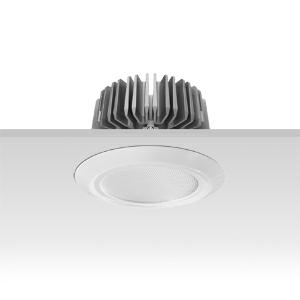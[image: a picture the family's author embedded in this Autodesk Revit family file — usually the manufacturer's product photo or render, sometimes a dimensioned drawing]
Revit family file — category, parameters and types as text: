
# Revit family: 3f_filippi_-_3f_reno_bianco_ampio_3f_filippi_-_30379_a01046_-_3f_reno_150_wh_2000-930_dali_wide___smp_wh_20f6
name_source: partatom
category: Lighting Fixtures
units: mm (PartAtom-declared; Revit-internal decimal feet)

## family parameters
Cut with Voids When Loaded = No
Host = Face
Light Source = No
Part Type = Normal
Room Calculation Point = No
Round Connector Dimension = Use Diameter
Shared = No

## types (1)
- 3F Filippi - 3F Reno Bianco Ampio (1 x LED, 1652 lm, 24 W, 3000 K)
    Apparent Load = 24 VA
    Approval mark = CE
    CIE Flux Codes = 73 92 98 100 100
    Color Rendering = 90
    Color Temperature = 3000 K
    Control Gear = Electronic transformer
    Default Elevation = 1800 mm
    Description = ILLUMINOTECHNICAL
Luminous efficiency 100% (DLOR 100%, ULOR 0%).
Initial luminous flux of the luminaire 1652 lm.
Direct symmetric wide distribution.
Installation Interdistance Transv.D = 1.01 x hu - Long.D = 1.00 x hu.
Tabular UGR (CIE 117 - 4H-8H; S=0.25H; 70/50/20): RUG 23.3 - 23.3.
Beam angle: 70° - 70°.
Luminous efficacy 69 lm/W.
Lifetime (L90/B10): 30000 h. (tq+25°C)
Lifetime (L85/B10): 50000 h. (tq+25°C)
Lifetime (L70/B10): 80000 h. (tq+25°C)
Sudden decreased luminous flux after 50000 hours: 0% (C0).
Photobiological safety in compliance with IEC/TR 62778: RG0 risk exempt, (IEC 62471).
In compliance with IEC/EN 62722-2-1 - IEC/EN 62717 standards.

SOURCE
Compact LED module 2000/930.
Energy efficiency class (UE 2019/2020 - UE 2019/2015): E.
CIE 13.3 Colour rendering index: CRI >90 (R9 >50%).
IES TM-30 Fidelity Index: Rf = 92 Rg = 101.
CCT nominal colour temperature 3000 K.
Colour initial tolerance (MacAdam): SDCM 3.
Zhaga Book 3 compliant.

MECHANICAL
Passive heat dissipator in die-casting aluminium, oversized, for optimum thermal management of the LED module.
Parabolic element with graduated/concentric rings in white polycarbonate.
Transparent external lens with glossy and satin differentiated surfaces, with a cooling and anti-insect system in methacrylate (PMMA).
Fastening spring clips in stainless steel.
Dimensions: diameter 176 mm, height 111 mm. Weight 0.79 kg.
IP44 protection degree for exposed part, IP20 for recessed part.
Mechanical strength to impacts IK05 (0.7 joule).
Glow-wire test resistance 650°C.

ELECTRICAL
Wiring on a separate unit.
Halogen Free DALI-2 DATI (Parts 251, 252, 253), PUSH-DIM, electronic wiring 230V-50/60Hz, power factor 0.95 at full load, THD <25%, constant output current, SELV, class II, 1 driver, 1 DALI addresse.
Power of the luminaire 24 W.
ENEC - CE.
SAFE FLICKER: PstLM=<1 and SVM=<0.4 (IEC TR 61547-1 and IEC TR 63158), to ensure a more comfortable and safe light.
Luminaire compliant with EN 60598-2-22 for power supply from a centralised emergency system CPSS (Central Power Supply System), not incorporated in the luminaire - high risk areas excluded. The default power and flux are 100% in AC and 100% in DC.
Ambient temperature from 0°C to +25°C.
Temperature class T6 max 85°C.
Relative humidity UR: <85%.

INSTALLATION
Pull-up recessed fitting.
False ceiling carving: 150 mm.
All accessories dedicated to this product are available on the Catalog and on our website www.3F-Filippi.com.

ACCESSORIES
A01046 - Anti-glare microprismatic SMP diffuser in methacrylate (PMMA), locked and in line with the trim, in white polycarbonate.

APPLICATIONS
Suitable product for food production plants (HACCP), IFS (Food Version 6), BRC (GSFS Food Version 7).
Environments: architectural, commercial, exhibition areas, transit areas, corridors, shops, display windows, service areas.
In false ceilings with narrow voids.

LIGHT MANAGEMENT
Recommended minimum setting: 10%.
The luminaire, equipped with (DALI-2 DATI) driver, can be controlled manually with 3F Easy Dim technology or automatically/manually with wired or wireless DALI/D2D control systems.
The D2D driver guarantees interoperability with other devices with the same certification by making the following information available:
Device Data (Part 251), Energy Report (Part 252), Diagnosis & Maintenance (Part 253).
In electrical systems without a regulation system (manual or automatic) and DALI bus, a suitable jumper must be made on the DA-DA terminals of the appliance.

WARNING
Luminaire designed for disposal/recycling at end-of-life.
Replaceable (LED only) light source by a professional. Replaceable control gear by a professional.
    Height = 0 mm  [stored 0 ft]
    Lamp = 1 x LED
    Lamp Light Flux = 1652 lm
    Lamp Power = 24 W
    Lamp count = 1
    Length = 176 mm
    Lifetime = 50000 h
    Luminous efficacy = 69 lm/W
    Manufacturer = 3F Filippi
    ModVariant = No
    Model = 3F Filippi - 30379+A01046 - 3F Reno 150 WH 2000-930 DALI WIDE + SMP WH
    Mounting Place = Ceiling
    Mounting Type = Recessed
    Number of Poles = 1
    OnlyDefault = Yes
    Power Factor = 1
    Product Name = 3F Filippi - 3F Reno Bianco Ampio
    Product group = recessed luminaire
    ProductGroupID = 4
    Protection Class = Protection class II
    Protection Degree = IP 20
    RLX_Detail_Level = 1
    RLX_Emergency_Light_Flux = 0 lm
    RLX_Emergency_Type = 0
    RLX_Emergency_Type_DB = No
    RlxData = <blob elided: 85785 chars, md5=7cec1c03>
    Socket = socket
    Standby Power = 0 W
    System Light Flux = 1652 lm
    System Power = 24 W
    Type Comments = Product without accessories
    Type Image = 3ffilippi_3f_reno_150_wh_vs_smp.jpg
    URL = http://relux.com
    VarID = ---
    Voltage = 0 V
    Weight = 0.00 kg
    Width = 0 mm  [stored 0 ft]

note: [stored X ft] marks values corroborated as IEEE doubles in the binary element streams (Revit-internal decimal feet)

## geometry (parser evidence)
native form markers: Blend x4, Sweep x10
no freeform markers — native parametric forms only
